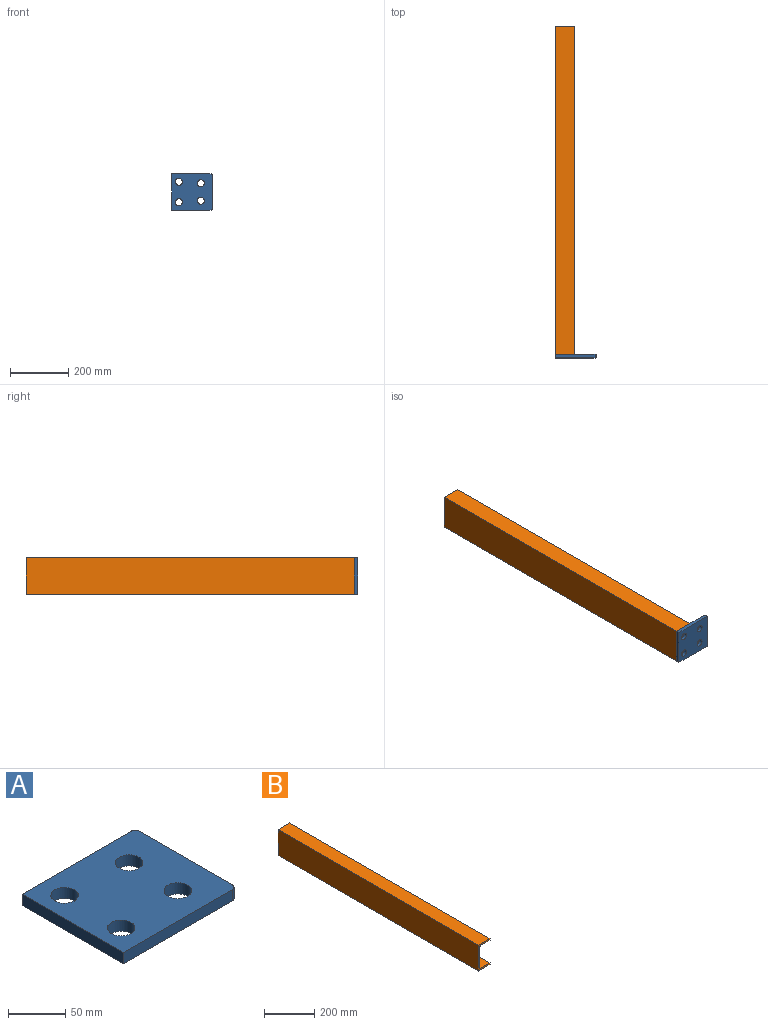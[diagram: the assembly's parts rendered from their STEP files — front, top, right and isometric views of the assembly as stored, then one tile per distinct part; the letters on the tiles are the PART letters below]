
ASSEMBLY  parts=2 mates=1
PART A: 12 faces, bbox 140x125x12 mm
  f0: plane 135x12mm, normal (0,1,0), area 1620mm2, adj f1,f8,f10,f11
  f1: plane 125x12mm, normal (-1,0,0), area 1500mm2, adj f0,f2,f10,f11
  f2: plane 135x12mm, normal (0,-1,0), area 1620mm2, adj f1,f3,f10,f11
  f3: cylinder r=5mm len=12mm, axis (0,0,-1), area 94.2mm2, adj f2,f4,f10,f11
  f4: plane 115x12mm, normal (1,0,0), area 1380mm2, adj f3,f8,f10,f11
  f5: cylinder r=12mm len=24mm, axis (0,0,-1), area 904.8mm2, adj f10,f11
  f6: cylinder r=12mm len=24mm, axis (0,0,-1), area 904.8mm2, adj f10,f11
  f7: cylinder r=12mm len=24mm, axis (0,0,-1), area 904.8mm2, adj f10,f11
  f8: cylinder r=5mm len=12mm, axis (0,0,-1), area 94.2mm2, adj f0,f4,f10,f11
  f9: cylinder r=12mm len=24mm, axis (0,0,-1), area 904.8mm2, adj f10,f11
  f10: plane 140x125mm, normal (0,0,1), area 15679.7mm2, adj f0,f1,f2,f3,f4,f5,f6,f7
  f11: plane 140x125mm, normal (0,0,-1), area 15679.7mm2, adj f0,f1,f2,f3,f4,f5,f6,f7
PART B: 12 faces, bbox 65x1123x125 mm
  f0: plane 1123x65mm, normal (0,0,1), area 72995mm2, adj f1,f9,f10,f11
  f1: plane 1123x125mm, normal (-1,0,0), area 140375mm2, adj f0,f2,f10,f11
  f2: plane 1123x65mm, normal (0,0,-1), area 72995mm2, adj f1,f3,f10,f11
  f3: plane 1123x7.5mm, normal (1,0,0), area 8422.5mm2, adj f2,f4,f10,f11
  f4: plane 1123x52.3mm, normal (0,0,1), area 58732.9mm2, adj f3,f5,f10,f11
  f5: cylinder r=8mm len=1123mm, axis (0,1,0), area 14112mm2, adj f4,f6,f10,f11
  f6: plane 1123x94mm, normal (1,0,0), area 105562mm2, adj f5,f7,f10,f11
  f7: cylinder r=8mm len=1123mm, axis (0,1,0), area 14112mm2, adj f6,f8,f10,f11
  f8: plane 1123x52.3mm, normal (0,0,-1), area 58732.9mm2, adj f7,f9,f10,f11
  f9: plane 1123x7.5mm, normal (1,0,0), area 8422.5mm2, adj f0,f8,f10,f11
  f10: plane 125x65mm, normal (0,-1,0), area 1519.5mm2, adj f0,f1,f2,f3,f4,f5,f6,f7
  f11: plane 125x65mm, normal (0,1,0), area 1519.5mm2, adj f0,f1,f2,f3,f4,f5,f6,f7
PLACE A rot(axis=(-1,0,0),90deg) t=(-500.05,-951.01,-139.56)mm
PLACE B t=(-500.05,183.99,-139.56)mm
MATE fastened A.f1 <-> B.f1  axis (-1,0,0) through (-525.22,-939.01,-139.56)mm
